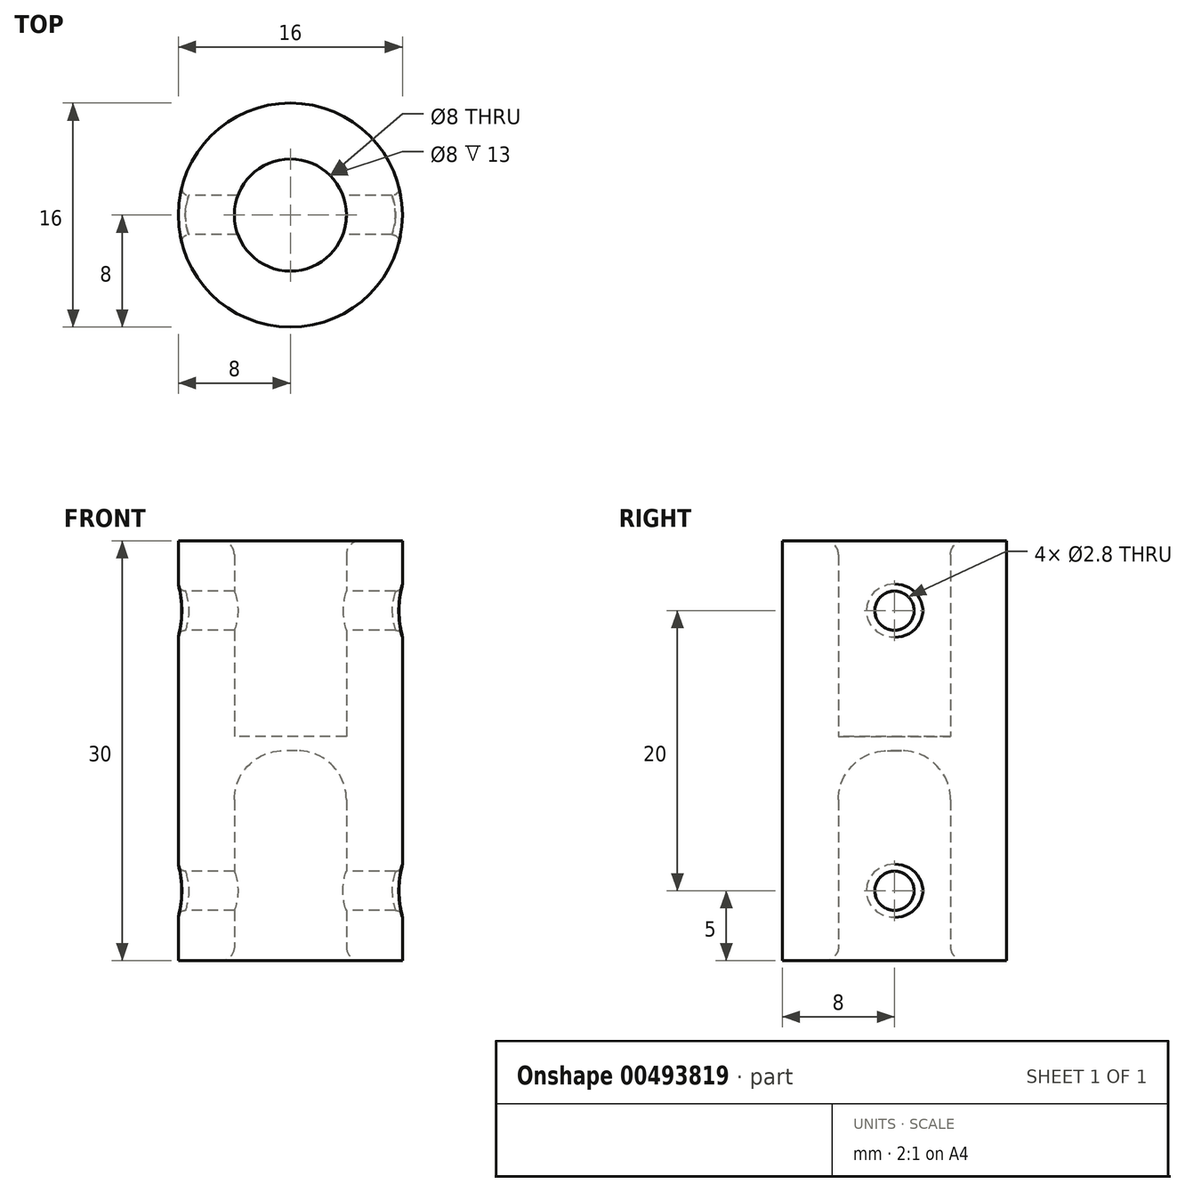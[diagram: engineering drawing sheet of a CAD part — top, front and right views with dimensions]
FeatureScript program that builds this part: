
annotation { "Feature Type Name" : "Feature", "Feature Type Description" : "" }
export const myFeature = defineFeature(function(context is Context, id is Id, definition is map)
    precondition{}
    {
        {
            var Q0;
            Q0=qCreatedBy(makeId("Top.planeOp"),FACE);
            var sketch = newSketch(context, id + "F0", { "sketchPlane" : qUnion([Q0])});
            skCircle(sketch, "E0", {"center": v(0, 0) * mm, "radius": 4 * mm});
            skCircle(sketch, "E1", {"center": v(0, 0) * mm, "radius": 8 * mm});
            skSolve(sketch);
        }
        {
            var Q0;
            Q0=makeQuery(id+"F0.imprint","IMPRINT",FACE,{"disambiguationData":[TD([[makeQuery(id+"F0.imprint","IMPRINT",EDGE,{"derivedFrom":sQuery(id+"F0.wireOp",EDGE,"E0")}),-1.0]])]});
            extrude(context, id + "F1", {"entities" : qUnion([Q0]), "depth" : 30 * mm});
        }
        {
            var Q0;
            Q0=qCreatedBy(makeId("Right.planeOp"),FACE);
            var sketch = newSketch(context, id + "F2", { "sketchPlane" : qUnion([Q0])});
            skCircle(sketch, "E2", {"center": v(0, 25) * mm, "radius": 1.4 * mm});
            skCircle(sketch, "E3", {"center": v(0, 5) * mm, "radius": 1.4 * mm});
            skSolve(sketch);
        }
        {
            var Q0;
            Q0=makeQuery(id+"F2.imprint","IMPRINT",FACE,{"disambiguationData":[TD([[makeQuery(id+"F2.imprint","IMPRINT",EDGE,{"derivedFrom":sQuery(id+"F2.wireOp",EDGE,"E2")}),1.0]])]});
            var Q1;
            Q1=makeQuery(id+"F2.imprint","IMPRINT",FACE,{"disambiguationData":[TD([[makeQuery(id+"F2.imprint","IMPRINT",EDGE,{"derivedFrom":sQuery(id+"F2.wireOp",EDGE,"E3")}),1.0]])]});
            extrude(context, id + "F3", {"entities" : qUnion([Q0, Q1]), "operationType" : NewBodyOperationType.REMOVE, "depth" : 8 * mm, "hasSecondDirection" : true, "secondDirectionOppositeDirection" : true, "secondDirectionDepth" : 8 * mm});
        }
        {
            var Q0;
            Q0=makeQuery(id+"F3.boolean.opBoolean","INTERSECT",EDGE,{"disambiguationData":[OD(1.0)],"derivedFrom":[makeQuery(id+"F1.opExtrude","SWEPT_FACE",FACE,{"disambiguationData":[OSD([sQuery(id+"F0.wireOp",EDGE,"E1")])]}),makeQuery(id+"F3.opExtrude","SWEPT_FACE",FACE,{"disambiguationData":[OSD([sQuery(id+"F2.wireOp",EDGE,"E3")])]})]});
            var Q1;
            Q1=makeQuery(id+"F3.boolean.opBoolean","INTERSECT",EDGE,{"disambiguationData":[OD(1.0)],"derivedFrom":[makeQuery(id+"F1.opExtrude","SWEPT_FACE",FACE,{"disambiguationData":[OSD([sQuery(id+"F0.wireOp",EDGE,"E1")])]}),makeQuery(id+"F3.opExtrude","SWEPT_FACE",FACE,{"disambiguationData":[OSD([sQuery(id+"F2.wireOp",EDGE,"E2")])]})]});
            var Q2;
            Q2=makeQuery(id+"F3.boolean.opBoolean","INTERSECT",EDGE,{"disambiguationData":[OD(0.0)],"derivedFrom":[makeQuery(id+"F1.opExtrude","SWEPT_FACE",FACE,{"disambiguationData":[OSD([sQuery(id+"F0.wireOp",EDGE,"E1")])]}),makeQuery(id+"F3.opExtrude","SWEPT_FACE",FACE,{"disambiguationData":[OSD([sQuery(id+"F2.wireOp",EDGE,"E2")])]})]});
            var Q3;
            Q3=makeQuery(id+"F3.boolean.opBoolean","INTERSECT",EDGE,{"disambiguationData":[OD(0.0)],"derivedFrom":[makeQuery(id+"F1.opExtrude","SWEPT_FACE",FACE,{"disambiguationData":[OSD([sQuery(id+"F0.wireOp",EDGE,"E1")])]}),makeQuery(id+"F3.opExtrude","SWEPT_FACE",FACE,{"disambiguationData":[OSD([sQuery(id+"F2.wireOp",EDGE,"E3")])]})]});
            fillet(context, id + "F4", {"entities" : qUnion([Q0, Q1, Q2, Q3]), "radius" : 0.5 * mm, "tangentPropagation" : true, "allowEdgeOverflow" : false});
        }
        {
            var Q0;
            Q0=makeQuery(id+"F1.opExtrude","CAP_EDGE",EDGE,{"disambiguationData":[OSD([sQuery(id+"F0.wireOp",EDGE,"E0")])],"isStart":false});
            var Q1;
            Q1=makeQuery(id+"F1.opExtrude","CAP_EDGE",EDGE,{"disambiguationData":[OSD([sQuery(id+"F0.wireOp",EDGE,"E0")])],"isStart":true});
            fillet(context, id + "F5", {"entities" : qUnion([Q0, Q1]), "radius" : 1 * mm, "tangentPropagation" : true, "allowEdgeOverflow" : false});
        }
        {
            var Q0;
            Q0=makeQuery(id+"F0.imprint","IMPRINT",FACE,{"disambiguationData":[TD([[makeQuery(id+"F0.imprint","IMPRINT",EDGE,{"derivedFrom":sQuery(id+"F0.wireOp",EDGE,"E0")}),1.0]])]});
            extrude(context, id + "F6", {"entities" : qUnion([Q0]), "operationType" : NewBodyOperationType.ADD, "depth" : 16 * mm, "hasSecondDirection" : true, "secondDirectionOppositeDirection" : false, "secondDirectionDepth" : 15 * mm});
        }
        {
            var Q0;
            Q0=makeQuery(id+"F6.opExtrude","CAP_EDGE",EDGE,{"disambiguationData":[OSD([sQuery(id+"F0.wireOp",EDGE,"E0")])],"isStart":true});
            fillet(context, id + "F7", {"entities" : qUnion([Q0]), "radius" : 3.5 * mm, "tangentPropagation" : true, "allowEdgeOverflow" : false});
        }
    });
